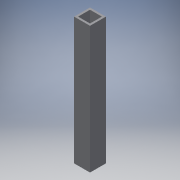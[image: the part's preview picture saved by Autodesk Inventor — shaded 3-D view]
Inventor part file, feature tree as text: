
AUTODESK INVENTOR PART (.ipt)
format: ipt  version: 2016 (Build 200138000, 138)  size: 114,176 bytes
history: native  units: in
note: dims shown in document units (in); Inventor stores cm internally (conversion verified against a paired STEP export)
features: extrude x2, sketch x2
ambient origin geometry x8: Origin, YZ Plane, XZ Plane, XY Plane, X Axis, Y Axis, Z Axis, Center Point
bodies: Solid1 (feature_tree)
feature tree (4):
  extrude  "Extrusion1"  Depth=1.0in
  extrude  "Extrusion2"  Depth=7.247in TaperAngle=0.0deg
  sketch  "Sketch1"  dims[d0=1.0in d1=1.0in]
  sketch  "Sketch2"  dims[d2=0.125in d3=7.247in d4=0.0in d5=0.2656in d6=0.5in d7=0.5in d8=0.2656in d9=0.5in d10=1.0in d11=0.2656in d12=1.0in d13=0.5in d14=1.0in d15=0.0in]
